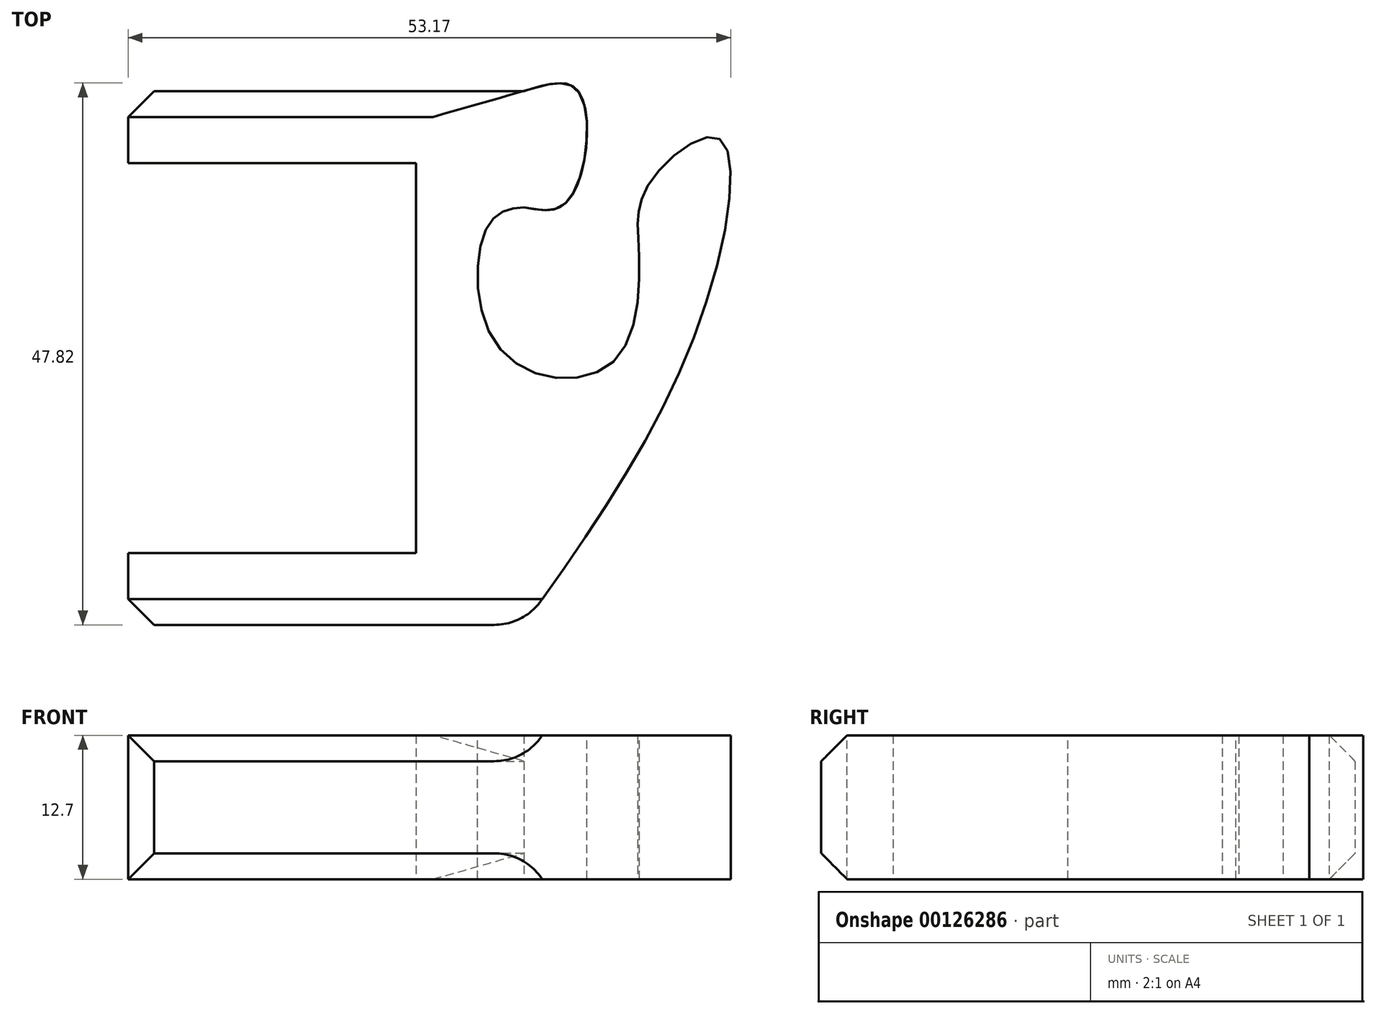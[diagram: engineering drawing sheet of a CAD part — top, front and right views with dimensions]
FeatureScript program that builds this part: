
annotation { "Feature Type Name" : "Feature", "Feature Type Description" : "" }
export const myFeature = defineFeature(function(context is Context, id is Id, definition is map)
    precondition{}
    {
        {
            var Q0;
            Q0=qCreatedBy(makeId("Top.planeOp"),FACE);
            var sketch = newSketch(context, id + "F0", { "sketchPlane" : qUnion([Q0])});
            skLineSegment(sketch, "E0", {"start": v(0, 0) * mm, "end": v(25.4, 0) * mm});
            skLineSegment(sketch, "E1", {"start": v(25.4, 0) * mm, "end": v(25.4, 34.42) * mm});
            skLineSegment(sketch, "E2", {"start": v(25.4, 34.42) * mm, "end": v(0, 34.42) * mm});
            skLineSegment(sketch, "E3", {"start": v(0, 34.42) * mm, "end": v(0, 40.77) * mm});
            skLineSegment(sketch, "E4", {"start": v(0, 40.77) * mm, "end": v(34.93, 40.77) * mm});
            skLineSegment(sketch, "E5", {"start": v(0, 0) * mm, "end": v(0, -6.35) * mm});
            skLineSegment(sketch, "E6", {"start": v(0, -6.35) * mm, "end": v(34.93, -6.35) * mm});
            skFitSpline(sketch, "E7", {"points": [v(34.93, -6.35) * mm, v(50.5, 20.58) * mm, v(51.97, 36.64) * mm, v(46.13, 32.85) * mm, v(44.96, 29.05) * mm], "startDerivative": vector(46.2, 64.84) * mm, "endDerivative": vector(-1.61, -24.99) * mm});
            skFitSpline(sketch, "E8", {"points": [v(34.93, 40.77) * mm, v(39.7, 40.77) * mm, v(38.83, 31.1) * mm, v(34.93, 30.51) * mm], "startDerivative": vector(18.08, 5.15) * mm, "endDerivative": vector(-14.59, 2.55) * mm});
            skFitSpline(sketch, "E9", {"points": [v(34.93, 30.51) * mm, v(31.81, 28.96) * mm, v(32.98, 17.81) * mm, v(43.2, 17.28) * mm, v(44.96, 29.05) * mm, v(45.04, 30.22) * mm], "startDerivative": vector(-24.2, -1.97) * mm, "endDerivative": vector(1.79, 9.44) * mm});
            skSolve(sketch);
        }
        {
            var Q0;
            Q0=makeQuery(id+"F0.imprint","IMPRINT",FACE,{"disambiguationData":[TD([[makeQuery(id+"F0.imprint","IMPRINT",EDGE,{"derivedFrom":sQuery(id+"F0.wireOp",EDGE,"E0")}),-1.0]])]});
            extrude(context, id + "F1", {"entities" : qUnion([Q0]), "depth" : 12.7 * mm});
        }
        {
            var Q0;
            Q0=makeQuery(id+"F1.opExtrude","CAP_EDGE",EDGE,{"disambiguationData":[OSD([sQuery(id+"F0.wireOp",EDGE,"E4")])],"isStart":false});
            var Q1;
            Q1=makeQuery(id+"F1.opExtrude","CAP_EDGE",EDGE,{"disambiguationData":[OSD([sQuery(id+"F0.wireOp",EDGE,"E4")])],"isStart":true});
            var Q2;
            Q2=makeQuery(id+"F1.opExtrude","SWEPT_EDGE",EDGE,{"disambiguationData":[OSD([sQuery(id+"F0.wireOp",EDGE,"E3"),sQuery(id+"F0.wireOp",EDGE,"E4")])]});
            var Q3;
            Q3=makeQuery(id+"F1.opExtrude","CAP_EDGE",EDGE,{"disambiguationData":[OSD([sQuery(id+"F0.wireOp",EDGE,"E6")])],"isStart":false});
            var Q4;
            Q4=makeQuery(id+"F1.opExtrude","SWEPT_EDGE",EDGE,{"disambiguationData":[OSD([sQuery(id+"F0.wireOp",EDGE,"E5"),sQuery(id+"F0.wireOp",EDGE,"E6")])]});
            var Q5;
            Q5=makeQuery(id+"F1.opExtrude","CAP_EDGE",EDGE,{"disambiguationData":[OSD([sQuery(id+"F0.wireOp",EDGE,"E6")])],"isStart":true});
            chamfer(context, id + "F2", {"entities" : qUnion([Q0, Q1, Q2, Q3, Q4, Q5]), "width" : 2.3 * mm, "tangentPropagation" : true});
        }
        {
            var Q0;
            Q0=makeQuery(id+"F1.opExtrude","SWEPT_EDGE",EDGE,{"disambiguationData":[OSD([sQuery(id+"F0.wireOp",EDGE,"E6"),sQuery(id+"F0.wireOp",EDGE,"E7")])]});
            fillet(context, id + "F3", {"entities" : qUnion([Q0]), "radius" : 5.08 * mm, "tangentPropagation" : true, "allowEdgeOverflow" : false});
        }
    });
